# Revit family: КШТ.61.103.ХХХ.Б
name_source: partatom
category: Pipe Accessories
revit_build: Autodesk Revit MEP 2015 (Build: 20140322_1515(x64)
units: mm (PartAtom-declared; Revit-internal decimal feet)

## types (8) — shared parameters
Description = Кран стальной шаровый, стандартнопроходной, фланцевый
Flange_h = 4 mm  [stored 0.0131234 ft]
K Coefficient = 0.31
Manufacturer = Броен
Model = Балломакс
Valve Material = <By Category>

## per-type parameters (varying)
| type | Assembly Code | DH | DN | Flange_B | Flange_D | Flange_D2 | Flange_R | Flange_R2 | H2 | L | RH | RN | Weight | ds | dv | i | rs | rs1 | rs2 | rv |
| DN300 PN16 | КШТ 61.103.300.Б | 426 mm | 300 mm | 32 mm  [stored 0.104987 ft] | 460 mm | 370 mm | 230 mm  [stored 0.754593 ft] | 185 mm  [stored 0.606955 ft] | 321 mm | 745 mm | 213 mm  [stored 0.698819 ft] | 150 mm | 165 | 50 mm  [stored 0.164042 ft] | 325 mm | 90 mm  [stored 0.295276 ft] | 25 mm  [stored 0.082021 ft] | 35 mm | 75 mm | 163 mm |
| DN300 PN25 | КШТ 61.103.300.Б | 426 mm | 300 mm | 36 mm  [stored 0.11811 ft] | 485 mm | 390 mm | 243 mm | 195 mm  [stored 0.639764 ft] | 321 mm | 745 mm | 213 mm  [stored 0.698819 ft] | 150 mm | 165 | 50 mm  [stored 0.164042 ft] | 325 mm | 90 mm  [stored 0.295276 ft] | 25 mm  [stored 0.082021 ft] | 35 mm | 75 mm | 163 mm |
| DN500 PN16 | КШТ 61.103.500.Б | 660 mm | 500 mm | 48 mm  [stored 0.15748 ft] | 710 mm | 585 mm | 355 mm | 293 mm | 459 mm | 1149 mm | 330 mm | 250 mm  [stored 0.82021 ft] | 503 | 80 mm  [stored 0.262467 ft] | 530 mm | 113 mm | 40 mm  [stored 0.131234 ft] | 50 mm  [stored 0.164042 ft] | 120 mm  [stored 0.393701 ft] | 265 mm  [stored 0.869423 ft] |
| DN500 PN25 | КШТ 61.103.500.Б | 660 mm | 500 mm | 52 mm | 730 mm | 615 mm | 365 mm | 308 mm | 459 mm | 1149 mm | 330 mm | 250 mm  [stored 0.82021 ft] | 503 | 80 mm  [stored 0.262467 ft] | 530 mm | 113 mm | 40 mm  [stored 0.131234 ft] | 50 mm  [stored 0.164042 ft] | 120 mm  [stored 0.393701 ft] | 265 mm  [stored 0.869423 ft] |
| DN400 PN16 | КШТ 61.103.400.Б | 508 mm | 400 mm | 38 mm  [stored 0.124672 ft] | 580 mm | 482 mm | 290 mm | 241 mm  [stored 0.790682 ft] | 355 mm | 955 mm | 254 mm | 200 mm  [stored 0.656168 ft] | 266 | 60 mm  [stored 0.19685 ft] | 426 mm | 100 mm  [stored 0.328084 ft] | 30 mm  [stored 0.0984252 ft] | 40 mm  [stored 0.131234 ft] | 90 mm  [stored 0.295276 ft] | 213 mm  [stored 0.698819 ft] |
| DN400 PN25 | КШТ 61.103.400.Б | 508 mm | 400 mm | 44 mm  [stored 0.144357 ft] | 610 mm | 505 mm | 305 mm | 253 mm | 355 mm | 955 mm | 254 mm | 200 mm  [stored 0.656168 ft] | 266 | 60 mm  [stored 0.19685 ft] | 426 mm | 100 mm  [stored 0.328084 ft] | 30 mm  [stored 0.0984252 ft] | 40 mm  [stored 0.131234 ft] | 90 mm  [stored 0.295276 ft] | 213 mm  [stored 0.698819 ft] |
| DN350 PN16 | КШТ 61.103.350.Б | 426 mm | 350 mm | 34 mm | 520 mm | 430 mm | 260 mm  [stored 0.853018 ft] | 215 mm | 321 mm | 824 mm | 213 mm  [stored 0.698819 ft] | 175 mm  [stored 0.574147 ft] | 210 | 50 mm  [stored 0.164042 ft] | 377 mm | 84 mm  [stored 0.275591 ft] | 25 mm  [stored 0.082021 ft] | 35 mm | 75 mm | 189 mm |
| DN350 PN25 | КШТ 61.103.350.Б | 426 mm | 350 mm | 42 mm  [stored 0.137795 ft] | 550 mm | 450 mm | 275 mm | 225 mm  [stored 0.738189 ft] | 321 mm | 824 mm | 213 mm  [stored 0.698819 ft] | 175 mm  [stored 0.574147 ft] | 210 | 50 mm  [stored 0.164042 ft] | 377 mm | 84 mm  [stored 0.275591 ft] | 25 mm  [stored 0.082021 ft] | 35 mm | 75 mm | 189 mm |

note: [stored X ft] marks values corroborated as IEEE doubles in the binary element streams (Revit-internal decimal feet)

## geometry (parser evidence)
native form markers: Sweep x2
no freeform markers — native parametric forms only
